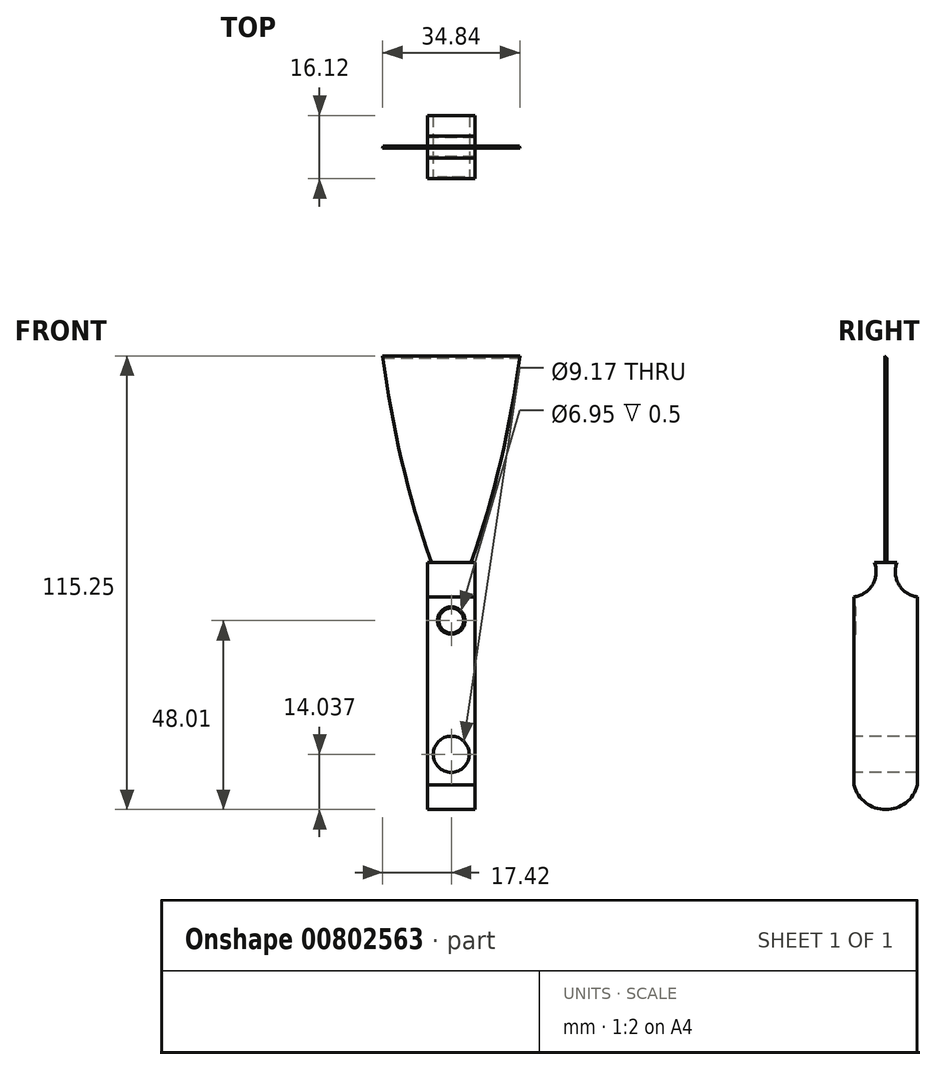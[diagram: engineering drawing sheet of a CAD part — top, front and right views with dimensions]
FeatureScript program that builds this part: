
annotation { "Feature Type Name" : "Feature", "Feature Type Description" : "" }
export const myFeature = defineFeature(function(context is Context, id is Id, definition is map)
    precondition{}
    {
        {
            var Q0;
            Q0=qCreatedBy(makeId("Front.planeOp"),FACE);
            var sketch = newSketch(context, id + "F0", { "sketchPlane" : qUnion([Q0])});
            skLineSegment(sketch, "E0", {"start": v(-17.95, 44.46) * mm, "end": v(17.95, 44.46) * mm});
            skArc(sketch, "E1", {"start": v(5.03, -12.54) * mm, "mid": v(13.1, 15.6) * mm, "end": v(17.95, 44.46) * mm});
            skLineSegment(sketch, "E2", {"start": v(0, 62.13) * mm, "end": v(0, -25.46) * mm});
            skArc(sketch, "E3.MirrorCS", {"start": v(-5.03, -12.54) * mm, "mid": v(-13.1, 15.6) * mm, "end": v(-17.95, 44.46) * mm});
            skLineSegment(sketch, "E4", {"start": v(-5.03, -12.54) * mm, "end": v(5.03, -12.54) * mm});
            skSolve(sketch);
        }
        {
            var Q0;
            Q0 = qSketchRegion(id + "F0", true);
            extrude(context, id + "F1", {"entities" : qUnion([Q0]), "endBound" : BoundingType.SYMMETRIC, "depth" : 0.5 * mm, "offsetDistance" : 25 * mm});
        }
        {
            var Q0;
            Q0=qCreatedBy(makeId("Right.planeOp"),FACE);
            var sketch = newSketch(context, id + "F2", { "sketchPlane" : qUnion([Q0])});
            skLineSegment(sketch, "E5", {"start": v(-2.85, -12.56) * mm, "end": v(0, -12.56) * mm});
            skLineSegment(sketch, "E6", {"start": v(0, -12.56) * mm, "end": v(2.85, -12.56) * mm});
            skArc(sketch, "E7", {"start": v(-8.06, -21.26) * mm, "mid": v(-3.36, -18.17) * mm, "end": v(-2.85, -12.56) * mm});
            skLineSegment(sketch, "E8", {"start": v(-8.06, -21.26) * mm, "end": v(-8.06, -69.1) * mm});
            skArc(sketch, "E9.MirrorCS", {"start": v(8.06, -21.26) * mm, "mid": v(3.36, -18.17) * mm, "end": v(2.85, -12.56) * mm});
            skLineSegment(sketch, "E10.MirrorCS", {"start": v(8.06, -21.26) * mm, "end": v(8.06, -69.1) * mm});
            skPoint(sketch, "E11.end.orphan", {"position": v(0, -75.27) * mm});
            skPoint(sketch, "E12.MirrorCS.start.orphan", {"position": v(8.06, -69.1) * mm});
            skArc(sketch, "E13", {"start": v(-8.06, -69.1) * mm, "mid": v(0, -75.3) * mm, "end": v(8.06, -69.1) * mm});
            skSolve(sketch);
        }
        {
            var Q0;
            Q0 = qSketchRegion(id + "F2", true);
            extrude(context, id + "F3", {"entities" : qUnion([Q0]), "endBound" : BoundingType.SYMMETRIC, "depth" : 12 * mm, "offsetDistance" : 25 * mm});
        }
        {
            var Q0;
            Q0=makeQuery(id+"F3.opExtrude","SWEPT_FACE",FACE,{"disambiguationData":[OSD([sQuery(id+"F2.wireOp",EDGE,"E8")])]});
            var sketch = newSketch(context, id + "F4", { "sketchPlane" : qUnion([Q0])});
            skCircle(sketch, "E14", {"center": v(0, -61.25) * mm, "radius": 4.59 * mm});
            skSolve(sketch);
        }
        {
            var Q0;
            Q0=makeQuery(id+"F4.imprint","IMPRINT",FACE,{"disambiguationData":[TD([[makeQuery(id+"F4.imprint","IMPRINT",EDGE,{"derivedFrom":sQuery(id+"F4.wireOp",EDGE,"E14")}),1.0]])]});
            extrude(context, id + "F5", {"entities" : qUnion([Q0]), "operationType" : NewBodyOperationType.REMOVE, "oppositeDirection" : true, "depth" : 17 * mm, "offsetDistance" : 25 * mm});
        }
        {
            var Q0;
            Q0=makeQuery(id+"F1.opExtrude","CAP_EDGE",EDGE,{"disambiguationData":[OSD([sQuery(id+"F0.wireOp",EDGE,"E0")])],"isStart":true});
            chamfer(context, id + "F6", {"entities" : qUnion([Q0]), "width" : 5 * mm, "tangentPropagation" : true});
        }
        {
            var Q0;
            Q0=makeQuery(id+"F3.opExtrude","SWEPT_FACE",FACE,{"disambiguationData":[OSD([sQuery(id+"F2.wireOp",EDGE,"E8")])]});
            var sketch = newSketch(context, id + "F7", { "sketchPlane" : qUnion([Q0])});
            skCircle(sketch, "E15", {"center": v(0, -27.28) * mm, "radius": 3.48 * mm});
            skSolve(sketch);
        }
        {
            var Q0;
            Q0=makeQuery(id+"F7.imprint","IMPRINT",FACE,{"disambiguationData":[TD([[makeQuery(id+"F7.imprint","IMPRINT",EDGE,{"derivedFrom":sQuery(id+"F7.wireOp",EDGE,"E15")}),1.0]])]});
            extrude(context, id + "F8", {"entities" : qUnion([Q0]), "operationType" : NewBodyOperationType.REMOVE, "oppositeDirection" : true, "depth" : 0.5 * mm, "offsetDistance" : 25 * mm});
        }
        {
            var Q0;
            Q0=makeQuery(id+"F8.boolean.opBoolean","COPY",FACE,{"derivedFrom":makeQuery(id+"F8.opExtrude","CAP_FACE",FACE,{"disambiguationData":[OSD([sQuery(id+"F7.wireOp",EDGE,"E15")])],"isStart":false})});
            var sketch = newSketch(context, id + "F9", { "sketchPlane" : qUnion([Q0])});
            skCircle(sketch, "E16", {"center": v(0, -27.28) * mm, "radius": 3.18 * mm});
            skSolve(sketch);
        }
        {
            var Q0;
            Q0 = qSketchRegion(id + "F9", true);
            extrude(context, id + "F10", {"entities" : qUnion([Q0]), "operationType" : NewBodyOperationType.ADD, "depth" : 0.5 * mm, "offsetDistance" : 25 * mm});
        }
        {
            var Q0;
            Q0 = qSketchRegion(id + "F9", true);
            extrude(context, id + "F11", {"entities" : qUnion([Q0]), "operationType" : NewBodyOperationType.ADD, "depth" : 0.5 * mm, "offsetDistance" : 25 * mm});
        }
    });
